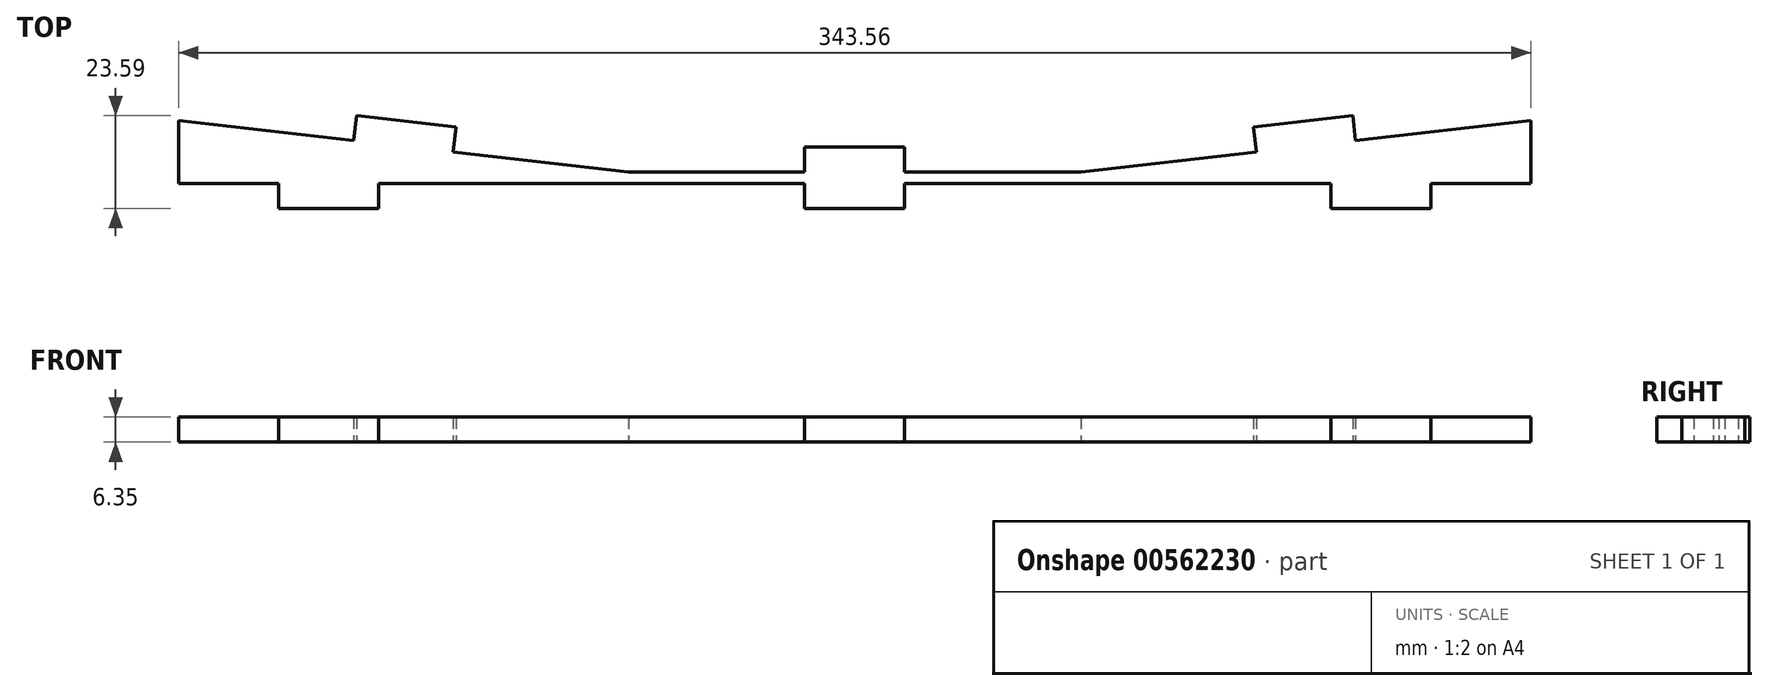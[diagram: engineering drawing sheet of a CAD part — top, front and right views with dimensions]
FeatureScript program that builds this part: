
annotation { "Feature Type Name" : "Feature", "Feature Type Description" : "" }
export const myFeature = defineFeature(function(context is Context, id is Id, definition is map)
    precondition{}
    {
        {
            var Q0;
            Q0=qCreatedBy(makeId("Top.planeOp"),FACE);
            var sketch = newSketch(context, id + "F0", { "sketchPlane" : qUnion([Q0])});
            skLineSegment(sketch, "E0", {"start": v(-171.78, 0) * mm, "end": v(171.78, 0) * mm});
            skLineSegment(sketch, "E1", {"start": v(-171.78, 0) * mm, "end": v(-171.78, 16) * mm});
            skLineSegment(sketch, "E2", {"start": v(-171.78, 16) * mm, "end": v(-57.5, 3) * mm});
            skLineSegment(sketch, "E3", {"start": v(-57.5, 3) * mm, "end": v(57.5, 3) * mm});
            skLineSegment(sketch, "E4", {"start": v(57.5, 3) * mm, "end": v(171.78, 16) * mm});
            skLineSegment(sketch, "E5", {"start": v(171.78, 16) * mm, "end": v(171.78, 0) * mm});
            skPoint(sketch, "E6.orphan", {"position": v(236.34, 0) * mm});
            skLineSegment(sketch, "E7", {"start": v(-146.38, 0) * mm, "end": v(-146.38, -6.35) * mm});
            skLineSegment(sketch, "E8", {"start": v(-146.38, -6.35) * mm, "end": v(-120.98, -6.35) * mm});
            skLineSegment(sketch, "E9", {"start": v(-120.98, -6.35) * mm, "end": v(-120.98, 0) * mm});
            skLineSegment(sketch, "E10", {"start": v(-12.7, 0) * mm, "end": v(-12.7, -6.35) * mm});
            skLineSegment(sketch, "E11", {"start": v(-12.7, -6.35) * mm, "end": v(12.7, -6.35) * mm});
            skLineSegment(sketch, "E12", {"start": v(12.7, -6.35) * mm, "end": v(12.7, 0) * mm});
            skLineSegment(sketch, "E13", {"start": v(146.38, 0) * mm, "end": v(146.38, -6.35) * mm});
            skLineSegment(sketch, "E14", {"start": v(146.38, -6.35) * mm, "end": v(120.98, -6.35) * mm});
            skLineSegment(sketch, "E15", {"start": v(120.98, -6.35) * mm, "end": v(120.98, 0) * mm});
            skLineSegment(sketch, "E16", {"start": v(-127.26, 10.94) * mm, "end": v(-126.54, 17.24) * mm});
            skLineSegment(sketch, "E17", {"start": v(-126.54, 17.24) * mm, "end": v(-101.3, 14.37) * mm});
            skLineSegment(sketch, "E18", {"start": v(-101.3, 14.37) * mm, "end": v(-102.02, 8.06) * mm});
            skLineSegment(sketch, "E19", {"start": v(-12.7, 3) * mm, "end": v(-12.7, 9.35) * mm});
            skLineSegment(sketch, "E20", {"start": v(-12.7, 9.35) * mm, "end": v(12.7, 9.35) * mm});
            skLineSegment(sketch, "E21", {"start": v(12.7, 9.35) * mm, "end": v(12.7, 3) * mm});
            skLineSegment(sketch, "E22", {"start": v(102.02, 8.06) * mm, "end": v(101.3, 14.37) * mm});
            skLineSegment(sketch, "E23", {"start": v(101.3, 14.37) * mm, "end": v(126.54, 17.24) * mm});
            skLineSegment(sketch, "E24", {"start": v(126.54, 17.24) * mm, "end": v(127.26, 10.94) * mm});
            skSolve(sketch);
        }
        {
            var Q0;
            Q0 = qSketchRegion(id + "F0", true);
            extrude(context, id + "F1", {"entities" : qUnion([Q0]), "depth" : 6.35 * mm, "offsetDistance" : 25.4 * mm});
        }
    });
